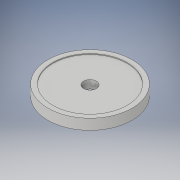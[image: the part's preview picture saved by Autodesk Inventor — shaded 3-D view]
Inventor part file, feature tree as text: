
AUTODESK INVENTOR PART (.ipt)
format: ipt  version: 2018 (Build 220112000, 112)  size: 112,128 bytes
history: native  units: mm
features: extrude x2, sketch x2
ambient origin geometry x8: Origin, YZ Plane, XZ Plane, XY Plane, X Axis, Y Axis, Z Axis, Center Point
bodies: Solid1 (feature_tree)
feature tree (4):
  extrude  "Extrusion1"  Depth=8.0mm
  extrude  "Extrusion2"  Depth=0.5mm
  sketch  "Sketch1"  dims[d0=46.0mm d1=8.0mm]
  sketch  "Sketch2"  dims[d2=5.0mm d3=0.0mm d4=52.0mm d5=6.0mm d6=0.5mm d7=0.0mm d8=0.0mm]
